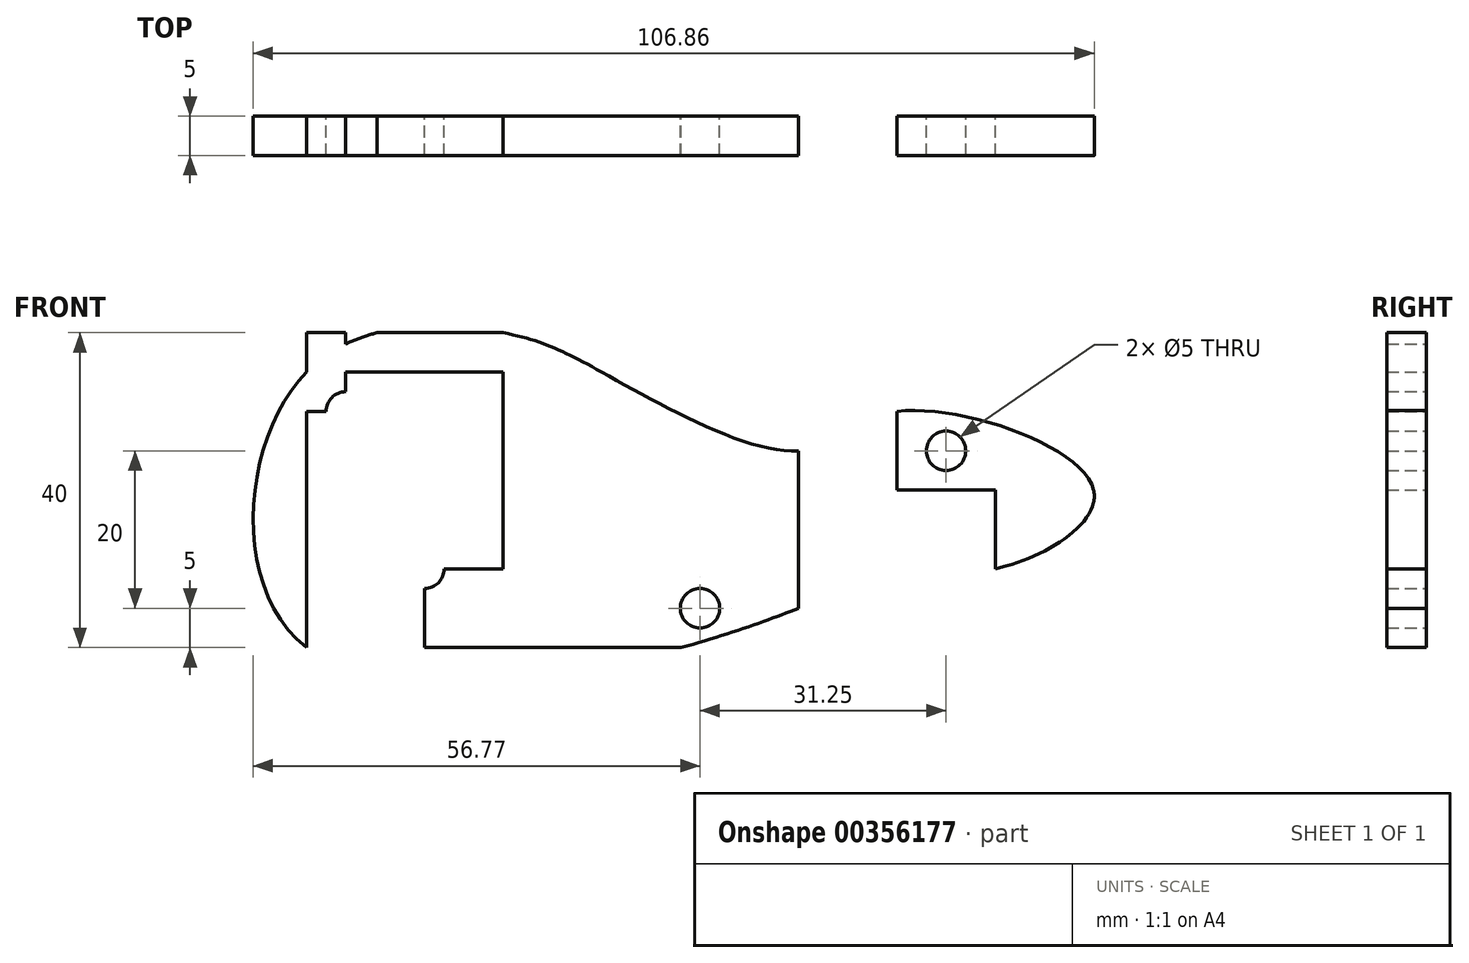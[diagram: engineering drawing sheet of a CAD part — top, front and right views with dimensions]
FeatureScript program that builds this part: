
annotation { "Feature Type Name" : "Feature", "Feature Type Description" : "" }
export const myFeature = defineFeature(function(context is Context, id is Id, definition is map)
    precondition{}
    {
        {
            var Q0;
            Q0=qCreatedBy(makeId("Front.planeOp"),FACE);
            var sketch = newSketch(context, id + "F0", { "sketchPlane" : qUnion([Q0])});
            skLineSegment(sketch, "E0.bottom", {"start": v(-50, 0) * mm, "end": v(50, 0) * mm});
            skLineSegment(sketch, "E0.top", {"start": v(-50, -40) * mm, "end": v(50, -40) * mm});
            skLineSegment(sketch, "E0.left", {"start": v(-50, 0) * mm, "end": v(-50, -40) * mm});
            skLineSegment(sketch, "E0.right", {"start": v(50, 0) * mm, "end": v(50, -40) * mm});
            skLineSegment(sketch, "E1", {"start": v(-50, -40) * mm, "end": v(-35, -40) * mm});
            skLineSegment(sketch, "E2", {"start": v(-50, -40) * mm, "end": v(-50, -30) * mm});
            skLineSegment(sketch, "E3", {"start": v(-50, -30) * mm, "end": v(-35, -30) * mm});
            skLineSegment(sketch, "E4", {"start": v(-35, -30) * mm, "end": v(-35, -40) * mm});
            skCircle(sketch, "E5", {"center": v(-35, -30) * mm, "radius": 2.5 * mm});
            skPoint(sketch, "E6", {"position": v(-45, -10) * mm});
            skLineSegment(sketch, "E7.bottom", {"start": v(-45, -10) * mm, "end": v(-50, -10) * mm});
            skLineSegment(sketch, "E7.top", {"start": v(-45, 0) * mm, "end": v(-50, 0) * mm});
            skLineSegment(sketch, "E7.left", {"start": v(-45, -10) * mm, "end": v(-45, 0) * mm});
            skLineSegment(sketch, "E7.right", {"start": v(-50, -10) * mm, "end": v(-50, 0) * mm});
            skCircle(sketch, "E8", {"center": v(-45, -10) * mm, "radius": 2.5 * mm});
            skPoint(sketch, "E9", {"position": v(0, 0) * mm});
            skPoint(sketch, "E10", {"position": v(50, -20) * mm});
            skLineSegment(sketch, "E11", {"start": v(0, 0) * mm, "end": v(50, 0) * mm});
            skPoint(sketch, "E12", {"position": v(25, 0) * mm});
            skLineSegment(sketch, "E13", {"start": v(25, 0) * mm, "end": v(25, -40) * mm});
            skPoint(sketch, "E14", {"position": v(25, -20) * mm});
            skLineSegment(sketch, "E15", {"start": v(25, -20) * mm, "end": v(50, -20) * mm});
            skPoint(sketch, "E16", {"position": v(37.5, -20) * mm});
            skLineSegment(sketch, "E17", {"start": v(37.5, -20) * mm, "end": v(37.5, -40) * mm});
            skPoint(sketch, "E18", {"position": v(37.5, -30) * mm});
            skLineSegment(sketch, "E19", {"start": v(-50, 0) * mm, "end": v(0, 0) * mm});
            skPoint(sketch, "E20", {"position": v(-25, 0) * mm});
            skLineSegment(sketch, "E21", {"start": v(25, 0) * mm, "end": v(25, -20) * mm});
            skPoint(sketch, "E22", {"position": v(25, -10) * mm});
            skLineSegment(sketch, "E23", {"start": v(0, 0) * mm, "end": v(25, 0) * mm});
            skPoint(sketch, "E24", {"position": v(12.5, 0) * mm});
            skPoint(sketch, "E25", {"position": v(12.5, -10) * mm});
            skLineSegment(sketch, "E26", {"start": v(12.5, -10) * mm, "end": v(12.5, -20) * mm});
            skPoint(sketch, "E27", {"position": v(12.5, -15) * mm});
            skPoint(sketch, "E28", {"position": v(25, -30) * mm});
            skLineSegment(sketch, "E29", {"start": v(25, -30) * mm, "end": v(25, -40) * mm});
            skPoint(sketch, "E30", {"position": v(25, -35) * mm});
            skPoint(sketch, "E31", {"position": v(12.5, -35) * mm});
            skLineSegment(sketch, "E32", {"start": v(-25, 0) * mm, "end": v(-25, -40) * mm});
            skPoint(sketch, "E33", {"position": v(-50, -20) * mm});
            skLineSegment(sketch, "E34", {"start": v(25, -20) * mm, "end": v(25, -30) * mm});
            skPoint(sketch, "E35", {"position": v(25, -25) * mm});
            skLineSegment(sketch, "E36", {"start": v(-25, 0) * mm, "end": v(0, 0) * mm});
            skPoint(sketch, "E37", {"position": v(-12.5, 0) * mm});
            skPoint(sketch, "E38", {"position": v(-50, -5) * mm});
            skLineSegment(sketch, "E39", {"start": v(-50, -5) * mm, "end": v(-12.5, -5) * mm});
            skFitSpline(sketch, "E40", {"points": [v(12.5, -35) * mm, v(25, -30) * mm, v(37.5, -30) * mm, v(50, -20) * mm, v(25, -10) * mm, v(12.5, -15) * mm, v(-12.5, -5) * mm, v(-25, 0) * mm, v(-50, -5) * mm, v(-50, -40) * mm, v(12.5, -35) * mm]});
            skLineSegment(sketch, "E41", {"start": v(25, -10) * mm, "end": v(37.5, -20) * mm});
            skPoint(sketch, "E42", {"position": v(31.25, -15) * mm});
            skCircle(sketch, "E43", {"center": v(31.25, -15) * mm, "radius": 2.5 * mm});
            skLineSegment(sketch, "E44", {"start": v(12.5, -20) * mm, "end": v(12.5, -35) * mm});
            skLineSegment(sketch, "E45", {"start": v(-35, -30) * mm, "end": v(12.5, -30) * mm});
            skPoint(sketch, "E46", {"position": v(0, -35) * mm});
            skCircle(sketch, "E47", {"center": v(0, -35) * mm, "radius": 2.5 * mm});
            skPoint(sketch, "E48", {"position": v(0, -30) * mm});
            skSolve(sketch);
        }
        {
            var Q0;
            {var subQ0=sQuery(id+"F0.wireOp",EDGE,"E40");var subQ1=sQuery(id+"F0.wireOp",EDGE,"E0.right");var subQ3=makeQuery(id+"F0.imprint","INTERSECT",VERTEX,{"derivedFrom":[subQ1,subQ0]});Q0=makeQuery(id+"F0.imprint","IMPRINT",FACE,{"disambiguationData":[TD([[makeQuery(id+"F0.imprint","IMPRINT",EDGE,{"disambiguationData":[TD([[subQ3,1.0]])],"derivedFrom":subQ1}),1.0]])]});}
            var Q1;
            {var subQ0=sQuery(id+"F0.wireOp",EDGE,"E40");var subQ1=sQuery(id+"F0.wireOp",EDGE,"E19");var subQ3=makeQuery(id+"F0.imprint","INTERSECT",VERTEX,{"derivedFrom":[subQ1,subQ0]});Q1=makeQuery(id+"F0.imprint","IMPRINT",FACE,{"disambiguationData":[TD([[makeQuery(id+"F0.imprint","IMPRINT",EDGE,{"disambiguationData":[TD([[subQ3,-1.0]])],"derivedFrom":subQ1}),1.0]])]});}
            var Q2;
            {var subQ0=sQuery(id+"F0.wireOp",EDGE,"E1");Q2=makeQuery(id+"F0.imprint","IMPRINT",FACE,{"disambiguationData":[TD([[makeQuery(id+"F0.imprint","IMPRINT",EDGE,{"derivedFrom":subQ0}),-1.0]])]});}
            var Q3;
            {var subQ0=sQuery(id+"F0.wireOp",EDGE,"E0.left");Q3=makeQuery(id+"F0.imprint","IMPRINT",FACE,{"disambiguationData":[TD([[makeQuery(id+"F0.imprint","IMPRINT",EDGE,{"derivedFrom":subQ0}),-1.0]])]});}
            var Q4;
            {var subQ0=sQuery(id+"F0.wireOp",EDGE,"E39");var subQ1=sQuery(id+"F0.wireOp",EDGE,"E7.left");var subQ2=makeQuery(id+"F0.imprint","INTERSECT",VERTEX,{"derivedFrom":[subQ1,subQ0]});Q4=makeQuery(id+"F0.imprint","IMPRINT",FACE,{"disambiguationData":[TD([[makeQuery(id+"F0.imprint","IMPRINT",EDGE,{"disambiguationData":[TD([[subQ2,-1.0]])],"derivedFrom":subQ1}),1.0]])]});}
            var Q5;
            {var subQ0=sQuery(id+"F0.wireOp",EDGE,"E40");var subQ3=sQuery(id+"F0.wireOp",EDGE,"E39");var subQ5=makeQuery(id+"F0.imprint","INTERSECT",VERTEX,{"derivedFrom":[subQ3,subQ0]});Q5=makeQuery(id+"F0.imprint","IMPRINT",FACE,{"disambiguationData":[TD([[makeQuery(id+"F0.imprint","IMPRINT",EDGE,{"disambiguationData":[TD([[subQ5,1.0]])],"derivedFrom":subQ3}),1.0]])]});}
            var Q6;
            {var subQ0=sQuery(id+"F0.wireOp",EDGE,"E40");var subQ2=sQuery(id+"F0.wireOp",EDGE,"E0.right");var subQ4=makeQuery(id+"F0.imprint","INTERSECT",VERTEX,{"derivedFrom":[subQ2,subQ0]});Q6=makeQuery(id+"F0.imprint","IMPRINT",FACE,{"disambiguationData":[TD([[makeQuery(id+"F0.imprint","IMPRINT",EDGE,{"disambiguationData":[TD([[subQ4,1.0]])],"derivedFrom":subQ0}),1.0]])]});}
            var Q7;
            {var subQ5=sQuery(id+"F0.wireOp",EDGE,"E1");Q7=makeQuery(id+"F0.imprint","IMPRINT",FACE,{"disambiguationData":[TD([[makeQuery(id+"F0.imprint","IMPRINT",EDGE,{"derivedFrom":subQ5}),1.0]])]});}
            var Q8;
            {var subQ0=sQuery(id+"F0.wireOp",EDGE,"E8");var subQ3=sQuery(id+"F0.wireOp",EDGE,"E7.left");var subQ4=makeQuery(id+"F0.imprint","INTERSECT",VERTEX,{"derivedFrom":[subQ3,subQ0]});Q8=makeQuery(id+"F0.imprint","IMPRINT",FACE,{"disambiguationData":[TD([[makeQuery(id+"F0.imprint","IMPRINT",EDGE,{"disambiguationData":[TD([[subQ4,-1.0]])],"derivedFrom":subQ3}),1.0]])]});}
            var Q9;
            {var subQ0=sQuery(id+"F0.wireOp",EDGE,"E41");var subQ3=sQuery(id+"F0.wireOp",EDGE,"E43");var subQ7=makeQuery(id+"F0.imprint","INTERSECT",VERTEX,{"disambiguationData":[OD(0.0)],"derivedFrom":[subQ0,subQ3]});Q9=makeQuery(id+"F0.imprint","IMPRINT",FACE,{"disambiguationData":[TD([[makeQuery(id+"F0.imprint","IMPRINT",EDGE,{"disambiguationData":[TD([[subQ7,1.0]])],"derivedFrom":subQ3}),-1.0]])]});}
            var Q10;
            {var subQ0=sQuery(id+"F0.wireOp",EDGE,"E39");var subQ1=sQuery(id+"F0.wireOp",EDGE,"E7.left");var subQ2=makeQuery(id+"F0.imprint","INTERSECT",VERTEX,{"derivedFrom":[subQ1,subQ0]});Q10=makeQuery(id+"F0.imprint","IMPRINT",FACE,{"disambiguationData":[TD([[makeQuery(id+"F0.imprint","IMPRINT",EDGE,{"disambiguationData":[TD([[subQ2,-1.0]])],"derivedFrom":subQ1}),-1.0]])]});}
            var Q11;
            {var subQ8=sQuery(id+"F0.wireOp",EDGE,"E34");Q11=makeQuery(id+"F0.imprint","IMPRINT",FACE,{"disambiguationData":[TD([[makeQuery(id+"F0.imprint","IMPRINT",EDGE,{"derivedFrom":subQ8}),-1.0]])]});}
            var Q12;
            {var subQ6=sQuery(id+"F0.wireOp",EDGE,"E0.left");Q12=makeQuery(id+"F0.imprint","IMPRINT",FACE,{"disambiguationData":[TD([[makeQuery(id+"F0.imprint","IMPRINT",EDGE,{"derivedFrom":subQ6}),1.0]])]});}
            var Q13;
            {var subQ0=sQuery(id+"F0.wireOp",EDGE,"E41");var subQ3=sQuery(id+"F0.wireOp",EDGE,"E43");var subQ4=makeQuery(id+"F0.imprint","INTERSECT",VERTEX,{"disambiguationData":[OD(0.0)],"derivedFrom":[subQ0,subQ3]});Q13=makeQuery(id+"F0.imprint","IMPRINT",FACE,{"disambiguationData":[TD([[makeQuery(id+"F0.imprint","IMPRINT",EDGE,{"disambiguationData":[TD([[subQ4,-1.0]])],"derivedFrom":subQ3}),-1.0]])]});}
            var Q14;
            {var subQ0=sQuery(id+"F0.wireOp",EDGE,"E34");Q14=makeQuery(id+"F0.imprint","IMPRINT",FACE,{"disambiguationData":[TD([[makeQuery(id+"F0.imprint","IMPRINT",EDGE,{"derivedFrom":subQ0}),1.0]])]});}
            var Q15;
            {var subQ5=sQuery(id+"F0.wireOp",EDGE,"E5");var subQ6=sQuery(id+"F0.wireOp",EDGE,"E4");var subQ7=makeQuery(id+"F0.imprint","INTERSECT",VERTEX,{"derivedFrom":[subQ6,subQ5]});Q15=makeQuery(id+"F0.imprint","IMPRINT",FACE,{"disambiguationData":[TD([[makeQuery(id+"F0.imprint","IMPRINT",EDGE,{"disambiguationData":[TD([[subQ7,-1.0]])],"derivedFrom":subQ5}),-1.0]])]});}
            var Q16;
            {var subQ5=sQuery(id+"F0.wireOp",EDGE,"E0.top");var subQ7=sQuery(id+"F0.wireOp",EDGE,"E32");var subQ8=makeQuery(id+"F0.imprint","INTERSECT",VERTEX,{"derivedFrom":[subQ5,subQ7]});Q16=makeQuery(id+"F0.imprint","IMPRINT",FACE,{"disambiguationData":[TD([[makeQuery(id+"F0.imprint","IMPRINT",EDGE,{"disambiguationData":[TD([[subQ8,-1.0]])],"derivedFrom":subQ5}),1.0]])]});}
            var Q17;
            {var subQ3=sQuery(id+"F0.wireOp",EDGE,"E26");var subQ12=sQuery(id+"F0.wireOp",EDGE,"E44");var subQ13=makeQuery(id+"F0.imprint","INTERSECT",VERTEX,{"derivedFrom":[subQ3,subQ12]});Q17=makeQuery(id+"F0.imprint","IMPRINT",FACE,{"disambiguationData":[TD([[makeQuery(id+"F0.imprint","IMPRINT",EDGE,{"disambiguationData":[TD([[subQ13,1.0]])],"derivedFrom":subQ3}),-1.0]])]});}
            extrude(context, id + "F1", {"entities" : qUnion([Q0, Q1, Q2, Q3, Q4, Q5, Q6, Q7, Q8, Q9, Q10, Q11, Q12, Q13, Q14, Q15, Q16, Q17]), "depth" : 5 * mm});
        }
    });
